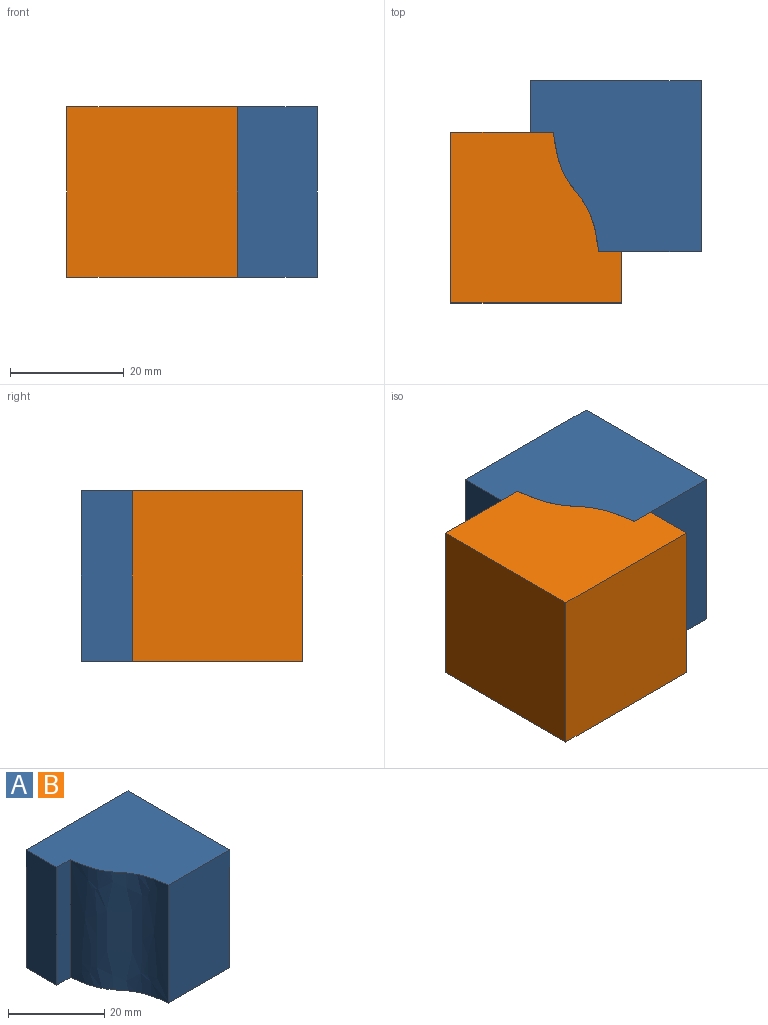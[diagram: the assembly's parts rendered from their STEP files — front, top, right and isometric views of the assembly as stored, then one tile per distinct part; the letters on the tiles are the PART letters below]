
ASSEMBLY  parts=2 mates=1
PART A: 8 faces, bbox 30x30x30 mm
  f0: plane 30x9mm, normal (-1,0,0), area 270mm2, adj f3,f4,f5,f7
  f1: plane 30x18mm, normal (0,-1,0), area 540mm2, adj f2,f4,f5,f6
  f2: plane 30x30mm, normal (1,0,0), area 900mm2, adj f1,f3,f4,f5
  f3: plane 30x30mm, normal (0,1,0), area 900mm2, adj f0,f2,f4,f5
  f4: plane 30x30mm, normal (0,0,1), area 732mm2, adj f0,f1,f2,f3,f6,f7
  f5: plane 30x30mm, normal (0,0,-1), area 732mm2, adj f0,f1,f2,f3,f6,f7
  f6: extruded ~30x21mm, area 686mm2, adj f1,f4,f5,f7
  f7: plane 30x4mm, normal (0,-1,0), area 120mm2, adj f0,f4,f5,f6
PART B: same geometry as A
PLACE A t=(12.59,-16.53,0)mm
PLACE B rot(axis=(0,0,1),180deg) t=(-31.41,4.47,0)mm
MATE fastened B.f7 <-> A.f1  axis (0,1,0) through (-5.41,-16.53,15)mm
